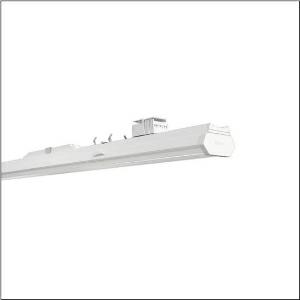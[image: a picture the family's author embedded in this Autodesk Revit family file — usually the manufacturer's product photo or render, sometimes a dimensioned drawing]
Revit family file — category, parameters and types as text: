
# Revit family: licross_21_protected_ho_52tp12mn4e5m
name_source: partatom
category: Lighting Fixtures
units: mm (PartAtom-declared; Revit-internal decimal feet)

## family parameters
Cut with Voids When Loaded = No
Host = Face
Light Source = No
Part Type = Normal
Room Calculation Point = No
Round Connector Dimension = Use Diameter
Shared = No

## types (1)
- --- (1 x LED, 14780 lm, 83.2 W, 4000K)
    Apparent Load = 83 VA
    CIE Flux Codes = 70 91 97 98 100
    Color Rendering = 80
    Color Temperature = 4000K
    Default Elevation = 1800 mm
    Description = Licross 21 Protected HO, luminaire insert, of sheet steel, galvanised, coil coated, white, length: 1.500mm, width: 90mm, height: 101mm, LED rated luminous flux: 14.790lm, light colour: 840, SDCM (Standard Deviation of Colour Matching)MacAdam ≤ 3 SDCM (initial), control gear: ON/OFF Multilumen, with plug, 3-pole, with phase selection, mains connection: 220..240V, AC, 50/60Hz, rated input power: 83W, internal wiring halogen-free, primary light control with lens, of plastic, primary optical cover: cover, of PMMA, light emission: direct distribution, primary light characteristic: symmetric, protection rating (complete): IP64, insulation class (complete): insulation class I (protective earthing), certification: CE, ENEC, VDE, UKCA, protection symbol: D if used in an environment with conductive dust loads with corresponding accessories, impact resistance: IK06, permissible ambient temperature for indoor applications: -35..+35°C, corresponds to IFS (International Featured Standards) requirements for safety and quality in the food industry, reducing of maximum allowable ambient temperature of 5°C with ceiling mounting, LABS conformity tested according to VDMA 24364:2018-05, The light source and the operating device comply with the requirements of the Ecodesign Regulation (EU) 2019/2020 and are replaceable in accordance with this regulation, packaging unit: 1 piece
    Height = 92 mm
    Lamp = 1 x LED
    Lamp Light Flux = 14780 lm
    Lamp Power = 83.2 W
    Lamp count = 1
    Length = 1500 mm
    Luminous efficacy = 178 lm/W
    Manufacturer = Siteco
    ModVariant = No
    Model = 52TP12MN4E5M
    Mounting Place = Ceiling
    Mounting Type = Pendant
    Number of Poles = 1
    OnlyDefault = Yes
    Power Factor = 1
    Product Name = Licross 21 Protected HO
    Product group = luminaire insert | ceiling pendant
    ProductGroupID = 901
    Protection Class = Protection class I
    Protection Degree = IP 64
    RLX_Detail_Level = 1
    RLX_Emergency_Light_Flux = 0 lm
    RLX_Emergency_Type = 0
    RLX_Emergency_Type_DB = No
    RlxData = <blob elided: 22313 chars, md5=279ec366>
    Socket = socket
    Standby Power = 0 W
    System Light Flux = 14780 lm
    System Power = 83 W
    Type Comments = factory setting: luminous flux: 100 % | (A | C | E) | 195 mA
    Type Image = l_1256148.jpg
    URL = http://relux.com
    VarID = @adj_109103
    Voltage = 0 V
    Weight = 0.00 kg
    Width = 88 mm

## geometry (parser evidence)
native form markers: Blend x4, Sweep x11
no freeform markers — native parametric forms only
